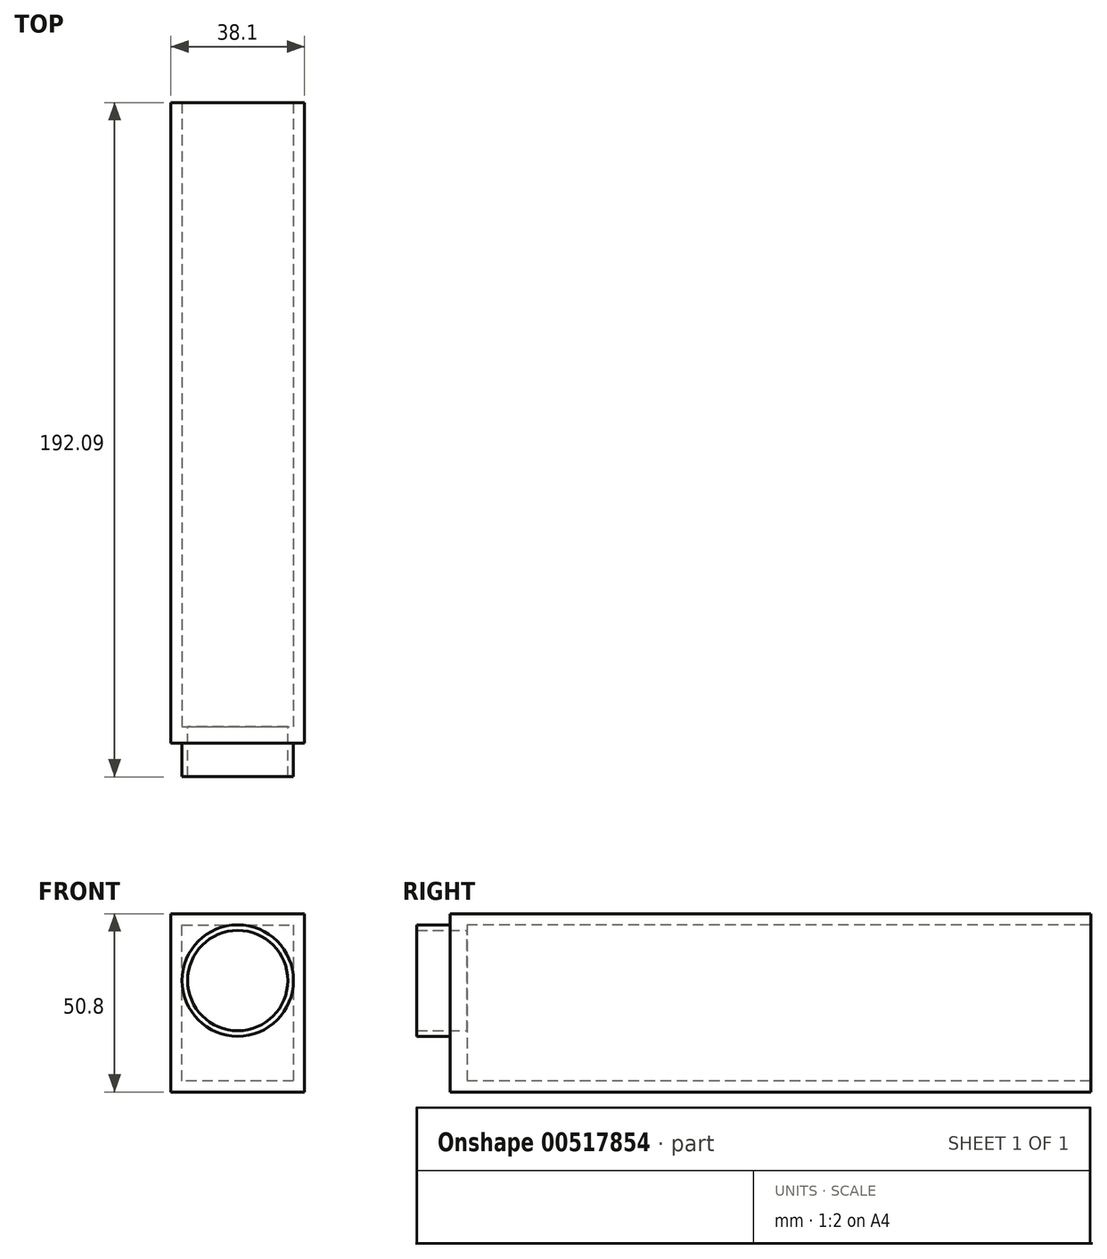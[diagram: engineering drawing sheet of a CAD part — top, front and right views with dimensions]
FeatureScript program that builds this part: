
annotation { "Feature Type Name" : "Feature", "Feature Type Description" : "" }
export const myFeature = defineFeature(function(context is Context, id is Id, definition is map)
    precondition{}
    {
        {
            var Q0;
            Q0=qCreatedBy(makeId("Front.planeOp"),FACE);
            var sketch = newSketch(context, id + "F0", { "sketchPlane" : qUnion([Q0])});
            skCircle(sketch, "E0", {"center": v(0, 0) * mm, "radius": 14.29 * mm});
            skCircle(sketch, "E1", {"center": v(0, 0) * mm, "radius": 15.88 * mm});
            skSolve(sketch);
        }
        {
            var Q0;
            Q0 = qSketchRegion(id + "F0", true);
            extrude(context, id + "F1", {"entities" : qUnion([Q0]), "depth" : 9.52 * mm, "offsetDistance" : 25.4 * mm});
        }
        {
            var Q0;
            Q0=qCreatedBy(makeId("Front.planeOp"),FACE);
            var sketch = newSketch(context, id + "F2", { "sketchPlane" : qUnion([Q0])});
            skCircle(sketch, "E2.0", {"center": v(0, 0) * mm, "radius": 14.29 * mm});
            skLineSegment(sketch, "E3", {"start": v(-19.05, 19.05) * mm, "end": v(-19.05, -31.75) * mm});
            skLineSegment(sketch, "E4", {"start": v(-19.05, -31.75) * mm, "end": v(19.05, -31.75) * mm});
            skLineSegment(sketch, "E5", {"start": v(19.05, -31.75) * mm, "end": v(19.05, 19.05) * mm});
            skLineSegment(sketch, "E6", {"start": v(19.05, 19.05) * mm, "end": v(-19.05, 19.05) * mm});
            skLineSegment(sketch, "E7", {"start": v(0, 36.3) * mm, "end": v(0, -49.77) * mm, "construction": true});
            skLineSegment(sketch, "E8", {"start": v(-50.32, 0) * mm, "end": v(38.4, 0) * mm, "construction": true});
            skSolve(sketch);
        }
        {
            var Q0;
            Q0 = qSketchRegion(id + "F2", true);
            extrude(context, id + "F3", {"entities" : qUnion([Q0]), "operationType" : NewBodyOperationType.ADD, "oppositeDirection" : true, "depth" : 4.76 * mm, "offsetDistance" : 25.4 * mm});
        }
        {
            var Q0;
            Q0=makeQuery(id+"F3.opExtrude","CAP_FACE",FACE,{"disambiguationData":[OSD([sQuery(id+"F2.wireOp",EDGE,"E2.0"),sQuery(id+"F2.wireOp",EDGE,"E3"),sQuery(id+"F2.wireOp",EDGE,"E4"),sQuery(id+"F2.wireOp",EDGE,"E5"),sQuery(id+"F2.wireOp",EDGE,"E6")])],"isStart":false});
            var sketch = newSketch(context, id + "F4", { "sketchPlane" : qUnion([Q0])});
            skLineSegment(sketch, "E9.0", {"start": v(-19.05, 19.05) * mm, "end": v(19.05, 19.05) * mm});
            skLineSegment(sketch, "E10.0", {"start": v(-19.05, -31.75) * mm, "end": v(-19.05, 19.05) * mm});
            skLineSegment(sketch, "E11.0", {"start": v(19.05, -31.75) * mm, "end": v(-19.05, -31.75) * mm});
            skLineSegment(sketch, "E12.0", {"start": v(19.05, 19.05) * mm, "end": v(19.05, -31.75) * mm});
            skLineSegment(sketch, "E13", {"start": v(-15.88, 15.88) * mm, "end": v(-15.88, -28.58) * mm});
            skLineSegment(sketch, "E14", {"start": v(-15.88, -28.58) * mm, "end": v(15.87, -28.57) * mm});
            skLineSegment(sketch, "E15", {"start": v(15.87, -28.57) * mm, "end": v(15.87, 15.88) * mm});
            skLineSegment(sketch, "E16", {"start": v(15.87, 15.88) * mm, "end": v(-15.88, 15.88) * mm});
            skSolve(sketch);
        }
        {
            var Q0;
            Q0 = qSketchRegion(id + "F4", true);
            extrude(context, id + "F5", {"entities" : qUnion([Q0]), "operationType" : NewBodyOperationType.ADD, "depth" : 177.8 * mm, "offsetDistance" : 25.4 * mm});
        }
    });
